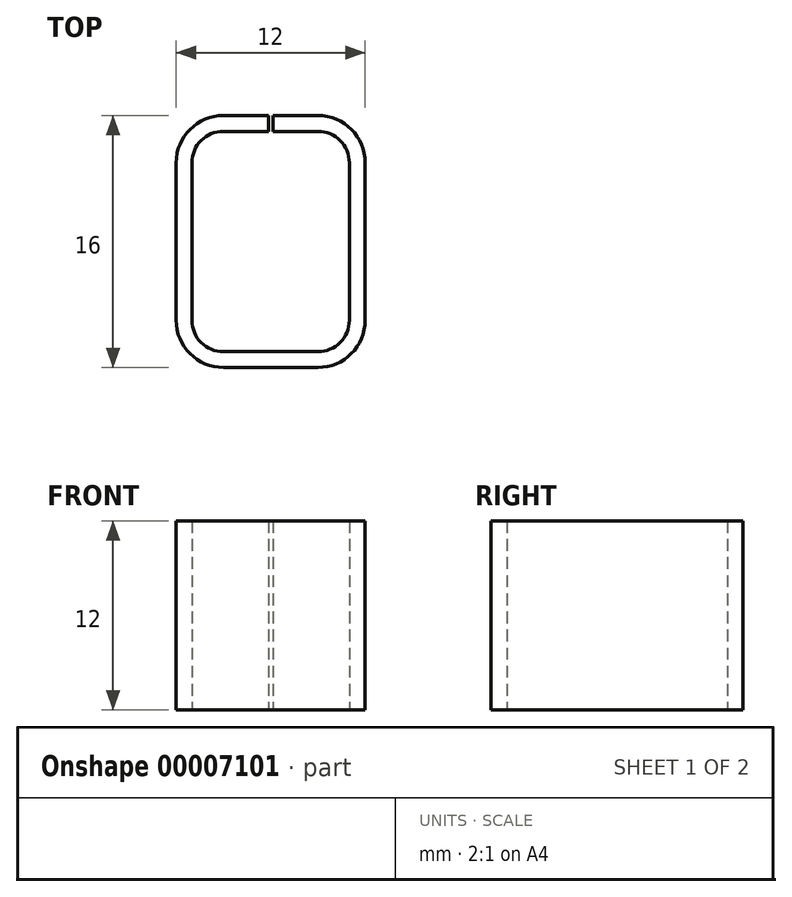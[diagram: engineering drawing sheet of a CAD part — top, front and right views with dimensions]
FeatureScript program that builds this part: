
annotation { "Feature Type Name" : "Feature", "Feature Type Description" : "" }
export const myFeature = defineFeature(function(context is Context, id is Id, definition is map)
    precondition{}
    {
        {
            var Q0;
            Q0=qCreatedBy(makeId("Top.planeOp"),FACE);
            var sketch = newSketch(context, id + "F0", { "sketchPlane" : qUnion([Q0])});
            skLineSegment(sketch, "E0.bottom", {"start": v(2, 0) * mm, "end": v(8, 0) * mm});
            skLineSegment(sketch, "E0.top", {"start": v(2, 14) * mm, "end": v(4.85, 14) * mm});
            skLineSegment(sketch, "E0.left", {"start": v(0, 2) * mm, "end": v(0, 12) * mm});
            skLineSegment(sketch, "E0.right", {"start": v(10, 2) * mm, "end": v(10, 12) * mm});
            skPoint(sketch, "E1.visualSharp", {"position": v(0, 14) * mm});
            skArc(sketch, "E1.filletArc", {"start": v(2, 14) * mm, "mid": v(0.59, 13.41) * mm, "end": v(0, 12) * mm});
            skPoint(sketch, "E2.visualSharp", {"position": v(10, 14) * mm});
            skArc(sketch, "E2.filletArc", {"start": v(10, 12) * mm, "mid": v(9.41, 13.41) * mm, "end": v(8, 14) * mm});
            skPoint(sketch, "E3.visualSharp", {"position": v(10, 0) * mm});
            skArc(sketch, "E3.filletArc", {"start": v(8, 0) * mm, "mid": v(9.41, 0.59) * mm, "end": v(10, 2) * mm});
            skPoint(sketch, "E4.visualSharp", {"position": v(0, 0) * mm});
            skArc(sketch, "E4.filletArc", {"start": v(0, 2) * mm, "mid": v(0.59, 0.59) * mm, "end": v(2, 0) * mm});
            skLineSegment(sketch, "E5.0", {"start": v(2, 15) * mm, "end": v(4.85, 15) * mm});
            skArc(sketch, "E5.1", {"start": v(11, 12) * mm, "mid": v(10.12, 14.12) * mm, "end": v(8, 15) * mm});
            skLineSegment(sketch, "E5.2", {"start": v(11, 2) * mm, "end": v(11, 12) * mm});
            skArc(sketch, "E5.3", {"start": v(8, -1) * mm, "mid": v(10.12, -0.12) * mm, "end": v(11, 2) * mm});
            skLineSegment(sketch, "E5.4", {"start": v(2, -1) * mm, "end": v(8, -1) * mm});
            skArc(sketch, "E5.5", {"start": v(2, 15) * mm, "mid": v(-0.12, 14.12) * mm, "end": v(-1, 12) * mm});
            skArc(sketch, "E5.6", {"start": v(-1, 2) * mm, "mid": v(-0.12, -0.12) * mm, "end": v(2, -1) * mm});
            skLineSegment(sketch, "E5.7", {"start": v(-1, 2) * mm, "end": v(-1, 12) * mm});
            skLineSegment(sketch, "E6", {"start": v(5, 14) * mm, "end": v(5, 0) * mm, "construction": true});
            skLineSegment(sketch, "E7", {"start": v(5.15, 14) * mm, "end": v(5.15, 15) * mm});
            skLineSegment(sketch, "E8.0.MirrorCS", {"start": v(4.85, 14) * mm, "end": v(4.85, 15) * mm});
            skPoint(sketch, "E9.orphan", {"position": v(5.15, 16.7) * mm});
            skPoint(sketch, "E10.orphan", {"position": v(4.85, 16.7) * mm});
            skPoint(sketch, "E11.orphan", {"position": v(4.85, 13.16) * mm});
            skPoint(sketch, "E12.orphan", {"position": v(5.15, 13.16) * mm});
            skLineSegment(sketch, "E13.trimOffspring", {"start": v(5.15, 14) * mm, "end": v(8, 14) * mm});
            skLineSegment(sketch, "E14.trimOffspring", {"start": v(5.15, 15) * mm, "end": v(8, 15) * mm});
            skSolve(sketch);
        }
        {
            var Q0;
            Q0 = qSketchRegion(id + "F0", true);
            extrude(context, id + "F1", {"entities" : qUnion([Q0]), "depth" : 12 * mm});
        }
    });
